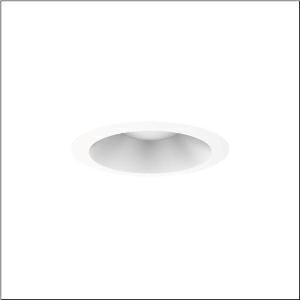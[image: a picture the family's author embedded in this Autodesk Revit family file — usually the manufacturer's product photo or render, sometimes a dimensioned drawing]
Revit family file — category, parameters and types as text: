
# Revit family: lunis_31_midi_51dn16dg42
name_source: partatom
category: Lighting Fixtures
units: mm (PartAtom-declared; Revit-internal decimal feet)

## family parameters
Cut with Voids When Loaded = No
Host = Face
Light Source = No
Part Type = Normal
Room Calculation Point = No
Round Connector Dimension = Use Diameter
Shared = No

## types (1)
- Lunis 31 midi (1 x LED, 2150 lm, 17 W, 4000K)
    Apparent Load = 17 VA
    CIE Flux Codes = 64 93 99 100 100
    Color Rendering = 80
    Color Temperature = 4000K
    Default Elevation = 1800 mm
    Description = Lunis 31,  midi, downlight, light control with reflector, light emission: direct distribution, LED rated luminous flux: 2.150lm, light colour: 840, mains connection: 220..240V, AC, 50/60Hz, housing, white, protection rating (complete): IP20, protection rating (on room side): IP54, insulation class (complete): insulation class II (safety insulation), certification: CE, packaging unit: 1 piece
    Height = 0 mm  [stored 0 ft]
    Lamp = 1 x LED
    Lamp Light Flux = 2150 lm
    Lamp Power = 17 W
    Lamp count = 1
    Length = 259 mm
    Luminous efficacy = 126 lm/W
    Manufacturer = Siteco
    ModVariant = No
    Model = 51DN16DG42
    Mounting Place = Ceiling
    Mounting Type = Recessed
    Number of Poles = 1
    OnlyDefault = Yes
    Power Factor = 1
    Product Name = Lunis 31 midi
    Product group = downlight
    ProductGroupID = 400
    Protection Class = Protection class II
    Protection Degree = IP 20
    RLX_Detail_Level = 1
    RLX_Emergency_Light_Flux = 0 lm
    RLX_Emergency_Type = 0
    RLX_Emergency_Type_DB = No
    RlxData = <blob elided: 23661 chars, md5=13815d84>
    Socket = socket
    Standby Power = 0 W
    System Light Flux = 2150 lm
    System Power = 17 W
    Type Comments = Product without accessories
    Type Image = l_1006711.jpg
    URL = http://relux.com
    VarID = ---
    Voltage = 0 V
    Weight = 0.00 kg
    Width = 0 mm  [stored 0 ft]

note: [stored X ft] marks values corroborated as IEEE doubles in the binary element streams (Revit-internal decimal feet)

## geometry (parser evidence)
native form markers: Blend x4, Sweep x11
no freeform markers — native parametric forms only
